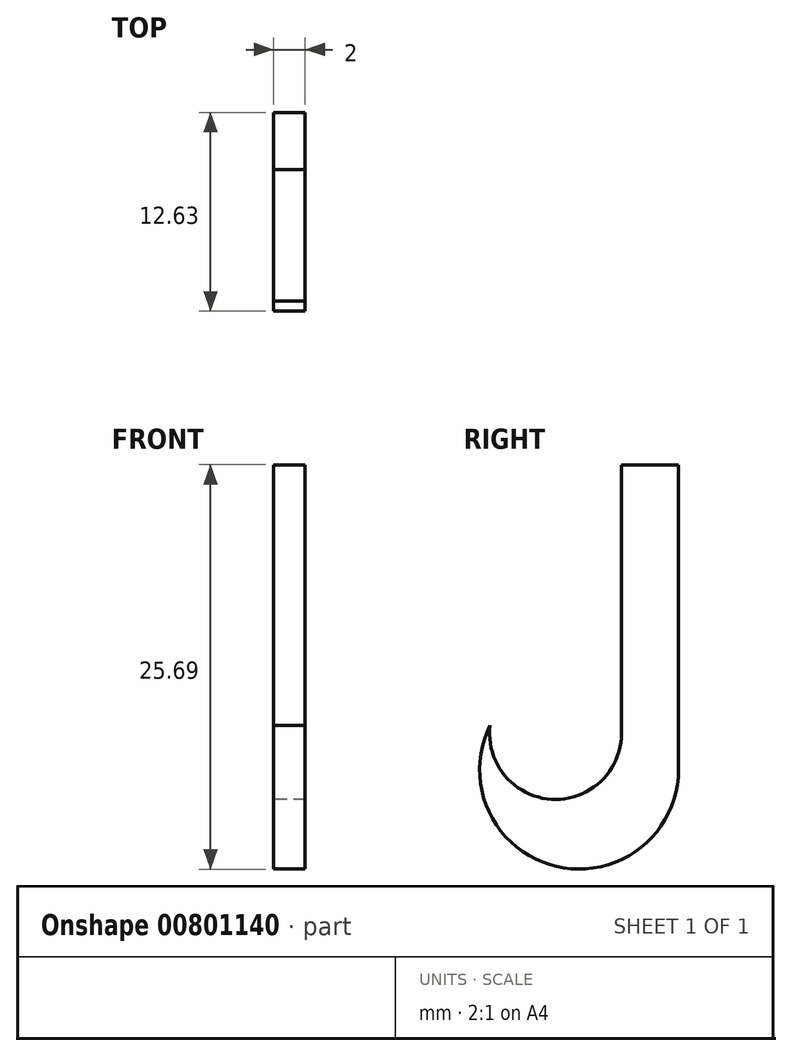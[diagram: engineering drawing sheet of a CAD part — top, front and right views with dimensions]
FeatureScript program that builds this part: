
annotation { "Feature Type Name" : "Feature", "Feature Type Description" : "" }
export const myFeature = defineFeature(function(context is Context, id is Id, definition is map)
    precondition{}
    {
        {
            var Q0;
            Q0=qCreatedBy(makeId("Right.planeOp"),FACE);
            var sketch = newSketch(context, id + "F0", { "sketchPlane" : qUnion([Q0])});
            skLineSegment(sketch, "E0", {"start": v(0, -12.63) * mm, "end": v(0, -32) * mm});
            skArc(sketch, "E1", {"start": v(-11.97, -29.18) * mm, "mid": v(-7.76, -38.15) * mm, "end": v(0, -32) * mm});
            skLineSegment(sketch, "E2", {"start": v(0, -12.63) * mm, "end": v(-3.63, -12.63) * mm});
            skLineSegment(sketch, "E3", {"start": v(-3.63, -12.63) * mm, "end": v(-3.63, -29.7) * mm});
            skArc(sketch, "E4", {"start": v(-11.97, -29.18) * mm, "mid": v(-8.08, -33.88) * mm, "end": v(-3.63, -29.7) * mm});
            skSolve(sketch);
        }
        {
            var Q0;
            Q0 = qSketchRegion(id + "F0", true);
            extrude(context, id + "F1", {"entities" : qUnion([Q0]), "depth" : 2 * mm, "offsetDistance" : 25 * mm});
        }
    });
